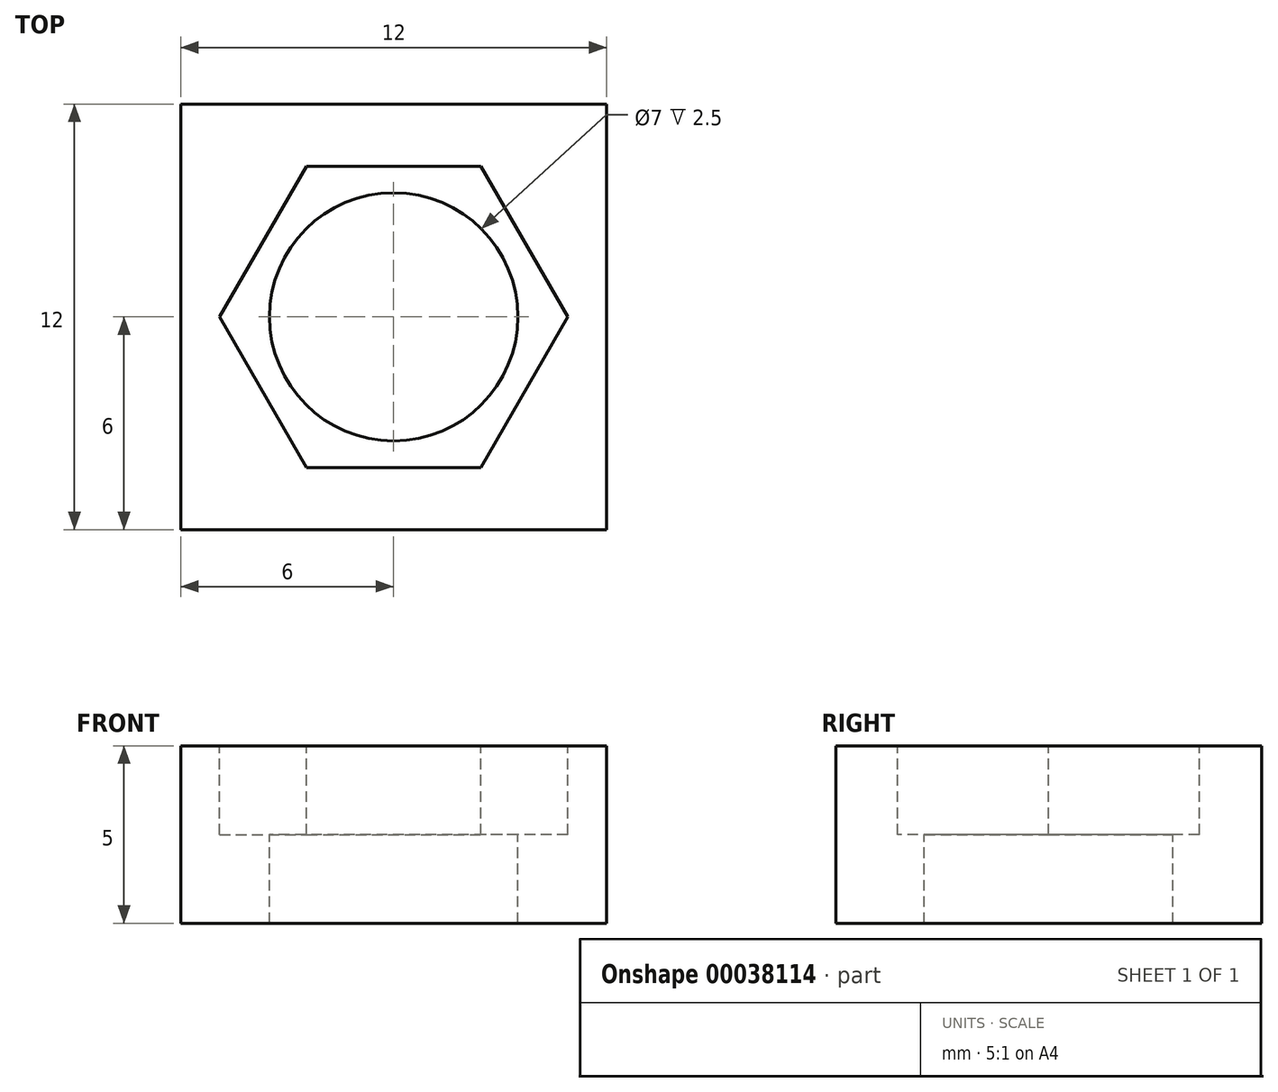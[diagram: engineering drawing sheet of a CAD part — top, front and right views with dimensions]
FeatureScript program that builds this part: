
annotation { "Feature Type Name" : "Feature", "Feature Type Description" : "" }
export const myFeature = defineFeature(function(context is Context, id is Id, definition is map)
    precondition{}
    {
        {
            var Q0;
            Q0=qCreatedBy(makeId("Top.planeOp"),FACE);
            var sketch = newSketch(context, id + "F0", { "sketchPlane" : qUnion([Q0])});
            skLineSegment(sketch, "E0.rect.bottom", {"start": v(6, -6) * mm, "end": v(-6, -6) * mm});
            skLineSegment(sketch, "E0.rect.top", {"start": v(6, 6) * mm, "end": v(-6, 6) * mm});
            skLineSegment(sketch, "E0.rect.left", {"start": v(6, -6) * mm, "end": v(6, 6) * mm});
            skLineSegment(sketch, "E0.rect.right", {"start": v(-6, -6) * mm, "end": v(-6, 6) * mm});
            skSolve(sketch);
        }
        {
            var Q0;
            Q0=makeQuery(id+"F0.imprint","IMPRINT",FACE,{"disambiguationData":[TD([[makeQuery(id+"F0.imprint","IMPRINT",EDGE,{"derivedFrom":sQuery(id+"F0.wireOp",EDGE,"E0.rect.bottom")}),-1.0]])]});
            extrude(context, id + "F1", {"entities" : qUnion([Q0]), "depth" : 5 * mm});
        }
        {
            var Q0;
            Q0=makeQuery(id+"F1.opExtrude","CAP_FACE",FACE,{"disambiguationData":[OSD([sQuery(id+"F0.wireOp",EDGE,"E0.rect.bottom"),sQuery(id+"F0.wireOp",EDGE,"E0.rect.top"),sQuery(id+"F0.wireOp",EDGE,"E0.rect.left"),sQuery(id+"F0.wireOp",EDGE,"E0.rect.right")])],"isStart":false});
            var sketch = newSketch(context, id + "F2", { "sketchPlane" : qUnion([Q0])});
            skCircle(sketch, "E1.cCircle", {"center": v(0, 0) * mm, "radius": 4.25 * mm, "construction": true});
            skLineSegment(sketch, "E1.0", {"start": v(4.9, 0) * mm, "end": v(2.45, -4.25) * mm});
            skLineSegment(sketch, "E1.1", {"start": v(2.45, -4.25) * mm, "end": v(-2.45, -4.25) * mm});
            skLineSegment(sketch, "E1.2", {"start": v(-2.45, -4.25) * mm, "end": v(-4.9, 0) * mm});
            skLineSegment(sketch, "E1.3", {"start": v(-4.9, 0) * mm, "end": v(-2.45, 4.25) * mm});
            skLineSegment(sketch, "E1.4", {"start": v(-2.45, 4.25) * mm, "end": v(2.45, 4.25) * mm});
            skLineSegment(sketch, "E1.5", {"start": v(2.45, 4.25) * mm, "end": v(4.9, 0) * mm});
            skPoint(sketch, "E1.0.midPoint", {"position": v(3.68, -2.12) * mm});
            skSolve(sketch);
        }
        {
            var Q0;
            Q0=makeQuery(id+"F2.imprint","IMPRINT",FACE,{"disambiguationData":[TD([[makeQuery(id+"F2.imprint","IMPRINT",EDGE,{"derivedFrom":sQuery(id+"F2.wireOp",EDGE,"E1.0")}),-1.0]])]});
            extrude(context, id + "F3", {"entities" : qUnion([Q0]), "operationType" : NewBodyOperationType.REMOVE, "oppositeDirection" : true, "depth" : 2.5 * mm});
        }
        {
            var Q0;
            Q0=makeQuery(id+"F3.boolean.opBoolean","COPY",FACE,{"derivedFrom":makeQuery(id+"F3.opExtrude","CAP_FACE",FACE,{"disambiguationData":[OSD([sQuery(id+"F2.wireOp",EDGE,"E1.0"),sQuery(id+"F2.wireOp",EDGE,"E1.1"),sQuery(id+"F2.wireOp",EDGE,"E1.2"),sQuery(id+"F2.wireOp",EDGE,"E1.3"),sQuery(id+"F2.wireOp",EDGE,"E1.4"),sQuery(id+"F2.wireOp",EDGE,"E1.5")])],"isStart":false})});
            var sketch = newSketch(context, id + "F4", { "sketchPlane" : qUnion([Q0])});
            skPoint(sketch, "E2", {"position": v(0, 0) * mm});
            skSolve(sketch);
        }
        {
            var Q0;
            Q0=sQuery(id+"F4.wireOp",VERTEX,"E2");
            var Q1;
            Q1=makeQuery(id+"F1.opExtrude","SWEPT_BODY",BODY,{"disambiguationData":[OSD([sQuery(id+"F0.wireOp",EDGE,"E0.rect.bottom"),sQuery(id+"F0.wireOp",EDGE,"E0.rect.top"),sQuery(id+"F0.wireOp",EDGE,"E0.rect.left"),sQuery(id+"F0.wireOp",EDGE,"E0.rect.right")])]});
            hole(context, id + "F5", {"style" : HoleStyle.SIMPLE, "holeDiameter" : 7 * mm, "endStyle" : HoleEndStyle.THROUGH, "locations" : qUnion([Q0]), "scope" : qUnion([Q1])});
        }
    });
